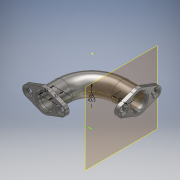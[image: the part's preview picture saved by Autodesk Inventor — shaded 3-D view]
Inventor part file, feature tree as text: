
AUTODESK INVENTOR PART (.ipt)
format: ipt  version: 2018 (Build 220112000, 112)  size: 312,320 bytes
history: native  units: mm
features: sketch x9, hole x4, sweep x2, extrude x2, plane x1
ambient origin geometry x8: Origin, YZ Plane, XZ Plane, XY Plane, X Axis, Y Axis, Z Axis, Center Point
bodies: Solid1 (feature_tree)
feature tree (18):
  sketch  "Sketch1"  dims[d15=43.5mm d16=32.0mm]
  plane  "Work Plane1"
  sweep  "Sweep1"
  sweep  "Sweep2"
  extrude  "Extrusion1"  Depth=135.75mm
  hole  "Hole1"  [1 undecoded]
  hole  "Hole2"  [1 undecoded]
  hole  "Hole3"  [1 undecoded]
  hole  "Hole4"  [1 undecoded]
  sketch  "Sketch2"  dims[d17=32.0mm d18=32.0mm]
  sketch  "Sketch3"  dims[d19=65.0mm d20=135.75mm]
  sketch  "Sketch4"  dims[d21=21.5mm d22=43.0mm]
  sketch  "Sketch5"  dims[d23=0.0mm d24=0.0mm d26=0.0mm d27=0.0mm]
  sketch  "Sketch6"  dims[d36=8.0mm d37=0.0mm]
  sketch  "Sketch8"  dims[d46=35.0mm]
  sketch  "Sketch9"  dims[d47=11.0mm d48=6.0mm d49=20.0mm d50=2.0mm d51=90.0deg d52=8.0mm d53=20.594885mm d55=0.0mm d56=8.0mm d57=95.0mm d58=35.0mm d59=6.0mm d60=40.0mm d61=2.0mm d62=90.0deg d63=8.0mm d64=20.594885mm d65=35.0mm d66=70.0mm d67=11.0mm d68=6.0mm d69=20.0mm d70=2.0mm d71=90.0deg d72=8.0mm d73=20.594885mm]
  sketch  "Sketch7"  dims[d38=35.0mm d39=6.0mm d40=40.0mm d41=2.0mm d42=90.0deg d43=8.0mm d44=20.594885mm d45=35.0mm]
  extrude  "Extrusion2"  Depth=95.0mm
note: 4 required parameter values undecoded (feature->parameter linkage not recoverable at this tier; creation-order binding heuristic only, values carry confidence <= 0.55)
